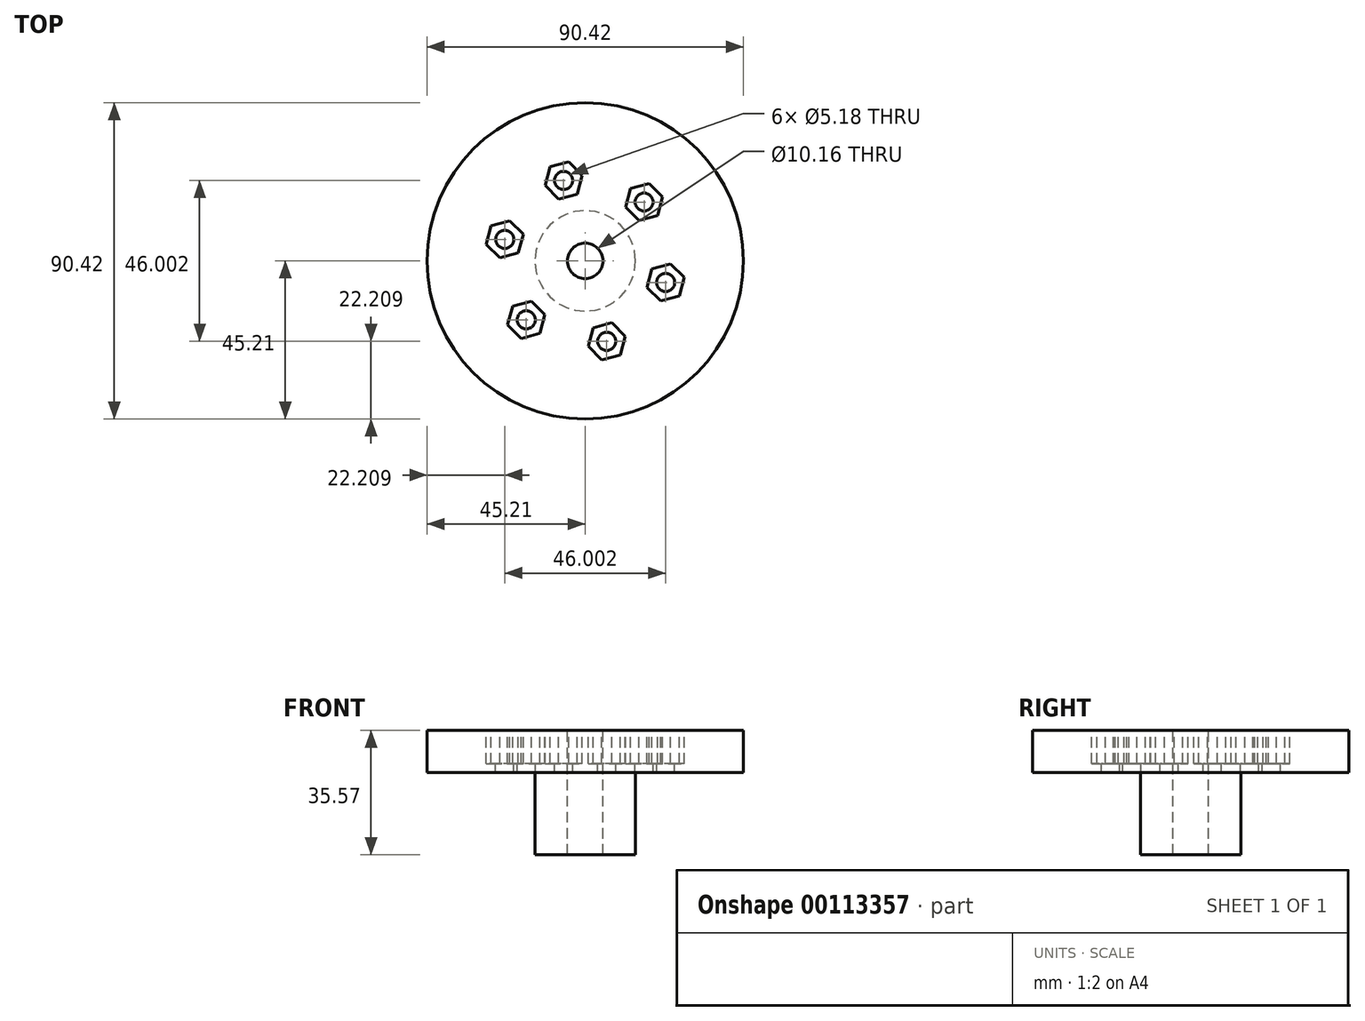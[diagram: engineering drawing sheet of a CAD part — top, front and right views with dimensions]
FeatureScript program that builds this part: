
annotation { "Feature Type Name" : "Feature", "Feature Type Description" : "" }
export const myFeature = defineFeature(function(context is Context, id is Id, definition is map)
    precondition{}
    {
        {
            var Q0;
            Q0=qCreatedBy(makeId("Top.planeOp"),FACE);
            var sketch = newSketch(context, id + "F0", { "sketchPlane" : qUnion([Q0])});
            skCircle(sketch, "E0", {"center": v(0, 0) * mm, "radius": 45.21 * mm});
            skSolve(sketch);
        }
        {
            var Q0;
            Q0=qSketchRegion(id+"F0",true);
            var Q1;
            Q1 = qSketchRegion(id + "F6", true);
            extrude(context, id + "F1", {"entities" : qUnion([Q0, Q1]), "depth" : 12.06 * mm, "offsetDistance" : 25.4 * mm});
        }
        {
            var Q0;
            Q0=makeQuery(id+"F1.opExtrude","CAP_FACE",FACE,{"disambiguationData":[OSD([sQuery(id+"F0.wireOp",EDGE,"E0")])],"isStart":false});
            var sketch = newSketch(context, id + "F2", { "sketchPlane" : qUnion([Q0])});
            skLineSegment(sketch, "E1", {"start": v(0, 0) * mm, "end": v(0, 60.06) * mm, "construction": true});
            skLineSegment(sketch, "E2", {"start": v(0, 0) * mm, "end": v(-13.99, 52.2) * mm, "construction": true});
            skCircle(sketch, "E3", {"center": v(0, 0) * mm, "radius": 23.81 * mm, "construction": true});
            skCircle(sketch, "E4", {"center": v(-6.16, 23) * mm, "radius": 2.6 * mm});
            skCircle(sketch, "E5.1.0", {"center": v(-23, 6.16) * mm, "radius": 2.6 * mm});
            skCircle(sketch, "E5.2.0", {"center": v(-16.84, -16.84) * mm, "radius": 2.6 * mm});
            skCircle(sketch, "E6.1.3.0", {"center": v(6.16, -23) * mm, "radius": 2.6 * mm});
            skCircle(sketch, "E6.1.4.0", {"center": v(23, -6.16) * mm, "radius": 2.6 * mm});
            skCircle(sketch, "E6.1.5.0", {"center": v(16.84, 16.84) * mm, "radius": 2.6 * mm});
            skLineSegment(sketch, "E7", {"start": v(0, 0) * mm, "end": v(16.84, 16.84) * mm, "construction": true});
            skSolve(sketch);
        }
        {
            var Q0;
            Q0=makeQuery(id+"F2.imprint","IMPRINT",FACE,{"disambiguationData":[TD([[makeQuery(id+"F2.imprint","IMPRINT",EDGE,{"derivedFrom":sQuery(id+"F2.wireOp",EDGE,"E4")}),1.0]])]});
            var Q1;
            Q1=makeQuery(id+"F2.imprint","IMPRINT",FACE,{"disambiguationData":[TD([[makeQuery(id+"F2.imprint","IMPRINT",EDGE,{"derivedFrom":sQuery(id+"F2.wireOp",EDGE,"E5.1.0")}),1.0]])]});
            var Q2;
            Q2=makeQuery(id+"F2.imprint","IMPRINT",FACE,{"disambiguationData":[TD([[makeQuery(id+"F2.imprint","IMPRINT",EDGE,{"derivedFrom":sQuery(id+"F2.wireOp",EDGE,"E5.2.0")}),1.0]])]});
            var Q3;
            Q3=makeQuery(id+"F2.imprint","IMPRINT",FACE,{"disambiguationData":[TD([[makeQuery(id+"F2.imprint","IMPRINT",EDGE,{"derivedFrom":sQuery(id+"F2.wireOp",EDGE,"E6.1.3.0")}),1.0]])]});
            var Q4;
            Q4=makeQuery(id+"F2.imprint","IMPRINT",FACE,{"disambiguationData":[TD([[makeQuery(id+"F2.imprint","IMPRINT",EDGE,{"derivedFrom":sQuery(id+"F2.wireOp",EDGE,"E6.1.4.0")}),1.0]])]});
            var Q5;
            Q5=makeQuery(id+"F2.imprint","IMPRINT",FACE,{"disambiguationData":[TD([[makeQuery(id+"F2.imprint","IMPRINT",EDGE,{"derivedFrom":sQuery(id+"F2.wireOp",EDGE,"E6.1.5.0")}),1.0]])]});
            extrude(context, id + "F3", {"entities" : qUnion([Q0, Q1, Q2, Q3, Q4, Q5]), "operationType" : NewBodyOperationType.REMOVE, "oppositeDirection" : true, "depth" : 25.4 * mm});
        }
        {
            var Q0;
            Q0=makeQuery(id+"F2.imprint","IMPRINT",FACE,{"disambiguationData":[TD([[makeQuery(id+"F2.imprint","IMPRINT",EDGE,{"derivedFrom":sQuery(id+"F2.wireOp",EDGE,"E4")}),-1.0]])]});
            var sketch = newSketch(context, id + "F4", { "sketchPlane" : qUnion([Q0])});
            skCircle(sketch, "E8", {"center": v(0, 0) * mm, "radius": 14.54 * mm});
            skSolve(sketch);
        }
        {
            var Q0;
            Q0=qSketchRegion(id+"F4",true);
            extrude(context, id + "F5", {"entities" : qUnion([Q0]), "operationType" : NewBodyOperationType.REMOVE, "oppositeDirection" : true, "depth" : 25.4 * mm});
        }
        {
            var Q0;
            Q0=makeQuery(id+"F1.opExtrude","CAP_FACE",FACE,{"disambiguationData":[OSD([sQuery(id+"F0.wireOp",EDGE,"E0")])],"isStart":false});
            var sketch = newSketch(context, id + "F6", { "sketchPlane" : qUnion([Q0])});
            skLineSegment(sketch, "E9", {"start": v(0, 0) * mm, "end": v(0, 45.21) * mm, "construction": true});
            skLineSegment(sketch, "E10", {"start": v(0, 0) * mm, "end": v(-11.7, 43.67) * mm, "construction": true});
            skLineSegment(sketch, "E11", {"start": v(0, 0) * mm, "end": v(31.97, 31.97) * mm, "construction": true});
            skLineSegment(sketch, "E12", {"start": v(0, 0) * mm, "end": v(43.67, -11.7) * mm, "construction": true});
            skLineSegment(sketch, "E13", {"start": v(0, 0) * mm, "end": v(11.7, -43.67) * mm, "construction": true});
            skLineSegment(sketch, "E14", {"start": v(0, 0) * mm, "end": v(-31.97, -31.97) * mm, "construction": true});
            skLineSegment(sketch, "E15", {"start": v(0, 0) * mm, "end": v(-43.67, 11.7) * mm, "construction": true});
            skCircle(sketch, "E16.cCircle", {"center": v(-6.16, 23) * mm, "radius": 4.76 * mm, "construction": true});
            skLineSegment(sketch, "E16.0", {"start": v(-10.05, 26.89) * mm, "end": v(-4.74, 28.31) * mm});
            skLineSegment(sketch, "E16.1", {"start": v(-4.74, 28.31) * mm, "end": v(-0.85, 24.42) * mm});
            skLineSegment(sketch, "E16.2", {"start": v(-0.85, 24.42) * mm, "end": v(-2.27, 19.11) * mm});
            skLineSegment(sketch, "E16.3", {"start": v(-2.27, 19.11) * mm, "end": v(-7.59, 17.69) * mm});
            skLineSegment(sketch, "E16.4", {"start": v(-7.59, 17.69) * mm, "end": v(-11.48, 21.58) * mm});
            skLineSegment(sketch, "E16.5", {"start": v(-11.48, 21.58) * mm, "end": v(-10.05, 26.89) * mm});
            skPoint(sketch, "E16.0.midPoint", {"position": v(-7.4, 27.6) * mm});
            skCircle(sketch, "E17.cCircle", {"center": v(16.84, 16.84) * mm, "radius": 4.76 * mm, "construction": true});
            skLineSegment(sketch, "E17.0", {"start": v(18.26, 22.15) * mm, "end": v(22.15, 18.26) * mm});
            skLineSegment(sketch, "E17.1", {"start": v(22.15, 18.26) * mm, "end": v(20.73, 12.95) * mm});
            skLineSegment(sketch, "E17.2", {"start": v(20.73, 12.95) * mm, "end": v(15.41, 11.53) * mm});
            skLineSegment(sketch, "E17.3", {"start": v(15.41, 11.53) * mm, "end": v(11.53, 15.41) * mm});
            skLineSegment(sketch, "E17.4", {"start": v(11.53, 15.41) * mm, "end": v(12.95, 20.73) * mm});
            skLineSegment(sketch, "E17.5", {"start": v(12.95, 20.73) * mm, "end": v(18.26, 22.15) * mm});
            skPoint(sketch, "E17.0.midPoint", {"position": v(20.2, 20.2) * mm});
            skCircle(sketch, "E18.cCircle", {"center": v(23, -6.16) * mm, "radius": 4.76 * mm, "construction": true});
            skLineSegment(sketch, "E18.0", {"start": v(28.31, -4.74) * mm, "end": v(26.89, -10.05) * mm});
            skLineSegment(sketch, "E18.1", {"start": v(26.89, -10.05) * mm, "end": v(21.58, -11.48) * mm});
            skLineSegment(sketch, "E18.2", {"start": v(21.58, -11.48) * mm, "end": v(17.69, -7.59) * mm});
            skLineSegment(sketch, "E18.3", {"start": v(17.69, -7.59) * mm, "end": v(19.11, -2.27) * mm});
            skLineSegment(sketch, "E18.4", {"start": v(19.11, -2.27) * mm, "end": v(24.42, -0.85) * mm});
            skLineSegment(sketch, "E18.5", {"start": v(24.42, -0.85) * mm, "end": v(28.31, -4.74) * mm});
            skPoint(sketch, "E18.0.midPoint", {"position": v(27.6, -7.4) * mm});
            skCircle(sketch, "E19.cCircle", {"center": v(6.16, -23) * mm, "radius": 4.76 * mm, "construction": true});
            skLineSegment(sketch, "E19.0", {"start": v(10.05, -26.89) * mm, "end": v(4.74, -28.31) * mm});
            skLineSegment(sketch, "E19.1", {"start": v(4.74, -28.31) * mm, "end": v(0.85, -24.42) * mm});
            skLineSegment(sketch, "E19.2", {"start": v(0.85, -24.42) * mm, "end": v(2.27, -19.11) * mm});
            skLineSegment(sketch, "E19.3", {"start": v(2.27, -19.11) * mm, "end": v(7.59, -17.69) * mm});
            skLineSegment(sketch, "E19.4", {"start": v(7.59, -17.69) * mm, "end": v(11.48, -21.58) * mm});
            skLineSegment(sketch, "E19.5", {"start": v(11.48, -21.58) * mm, "end": v(10.05, -26.89) * mm});
            skPoint(sketch, "E19.0.midPoint", {"position": v(7.4, -27.6) * mm});
            skCircle(sketch, "E20.cCircle", {"center": v(-16.84, -16.84) * mm, "radius": 4.76 * mm, "construction": true});
            skLineSegment(sketch, "E20.0", {"start": v(-18.26, -22.15) * mm, "end": v(-22.15, -18.26) * mm});
            skLineSegment(sketch, "E20.1", {"start": v(-22.15, -18.26) * mm, "end": v(-20.73, -12.95) * mm});
            skLineSegment(sketch, "E20.2", {"start": v(-20.73, -12.95) * mm, "end": v(-15.41, -11.53) * mm});
            skLineSegment(sketch, "E20.3", {"start": v(-15.41, -11.53) * mm, "end": v(-11.53, -15.41) * mm});
            skLineSegment(sketch, "E20.4", {"start": v(-11.53, -15.41) * mm, "end": v(-12.95, -20.73) * mm});
            skLineSegment(sketch, "E20.5", {"start": v(-12.95, -20.73) * mm, "end": v(-18.26, -22.15) * mm});
            skPoint(sketch, "E20.0.midPoint", {"position": v(-20.2, -20.2) * mm});
            skCircle(sketch, "E21.cCircle", {"center": v(-23, 6.16) * mm, "radius": 4.76 * mm, "construction": true});
            skLineSegment(sketch, "E21.0", {"start": v(-28.31, 4.74) * mm, "end": v(-26.89, 10.05) * mm});
            skLineSegment(sketch, "E21.1", {"start": v(-26.89, 10.05) * mm, "end": v(-21.58, 11.48) * mm});
            skLineSegment(sketch, "E21.2", {"start": v(-21.58, 11.48) * mm, "end": v(-17.69, 7.59) * mm});
            skLineSegment(sketch, "E21.3", {"start": v(-17.69, 7.59) * mm, "end": v(-19.11, 2.27) * mm});
            skLineSegment(sketch, "E21.4", {"start": v(-19.11, 2.27) * mm, "end": v(-24.42, 0.85) * mm});
            skLineSegment(sketch, "E21.5", {"start": v(-24.42, 0.85) * mm, "end": v(-28.31, 4.74) * mm});
            skPoint(sketch, "E21.0.midPoint", {"position": v(-27.6, 7.4) * mm});
            skSolve(sketch);
        }
        {
            var Q0;
            Q0=qSketchRegion(id+"F6",true);
            extrude(context, id + "F7", {"entities" : qUnion([Q0]), "operationType" : NewBodyOperationType.REMOVE, "oppositeDirection" : true, "depth" : 9.52 * mm, "offsetDistance" : 25.4 * mm});
        }
        {
            var Q0;
            Q0=makeQuery(id+"F1.opExtrude","CAP_FACE",FACE,{"disambiguationData":[OSD([sQuery(id+"F0.wireOp",EDGE,"E0")])],"isStart":false});
            var sketch = newSketch(context, id + "F8", { "sketchPlane" : qUnion([Q0])});
            skCircle(sketch, "E22", {"center": v(0, 0) * mm, "radius": 15.24 * mm});
            skSolve(sketch);
        }
        {
            var Q0;
            Q0 = qSketchRegion(id + "F8", true);
            extrude(context, id + "F9", {"entities" : qUnion([Q0]), "operationType" : NewBodyOperationType.ADD, "oppositeDirection" : true, "depth" : 12.06 * mm, "offsetDistance" : 25.4 * mm});
        }
        {
            var Q0;
            Q0=makeQuery(id+"F9.boolean.opBoolean","MERGE",FACE,{"derivedFrom":[makeQuery(id+"F1.opExtrude","CAP_FACE",FACE,{"disambiguationData":[OSD([sQuery(id+"F0.wireOp",EDGE,"E0")])],"isStart":false}),makeQuery(id+"F9.opExtrude","CAP_FACE",FACE,{"disambiguationData":[OSD([sQuery(id+"F8.wireOp",EDGE,"E22")])],"isStart":true})]});
            var sketch = newSketch(context, id + "F10", { "sketchPlane" : qUnion([Q0])});
            skCircle(sketch, "E23", {"center": v(0, 0) * mm, "radius": 14.35 * mm});
            skSolve(sketch);
        }
        {
            var Q0;
            Q0 = qSketchRegion(id + "F10", true);
            extrude(context, id + "F11", {"entities" : qUnion([Q0]), "operationType" : NewBodyOperationType.ADD, "oppositeDirection" : true, "depth" : 35.56 * mm, "offsetDistance" : 25.4 * mm});
        }
        {
            var Q0;
            Q0=makeQuery(id+"F9.boolean.opBoolean","MERGE",FACE,{"derivedFrom":[makeQuery(id+"F1.opExtrude","CAP_FACE",FACE,{"disambiguationData":[OSD([sQuery(id+"F0.wireOp",EDGE,"E0")])],"isStart":false}),makeQuery(id+"F9.opExtrude","CAP_FACE",FACE,{"disambiguationData":[OSD([sQuery(id+"F8.wireOp",EDGE,"E22")])],"isStart":true})]});
            var sketch = newSketch(context, id + "F12", { "sketchPlane" : qUnion([Q0])});
            skCircle(sketch, "E24", {"center": v(0, 0) * mm, "radius": 5.08 * mm});
            skSolve(sketch);
        }
        {
            var Q0;
            Q0 = qSketchRegion(id + "F12", true);
            extrude(context, id + "F13", {"entities" : qUnion([Q0]), "operationType" : NewBodyOperationType.REMOVE, "oppositeDirection" : true, "depth" : 38.1 * mm, "offsetDistance" : 25.4 * mm});
        }
    });
